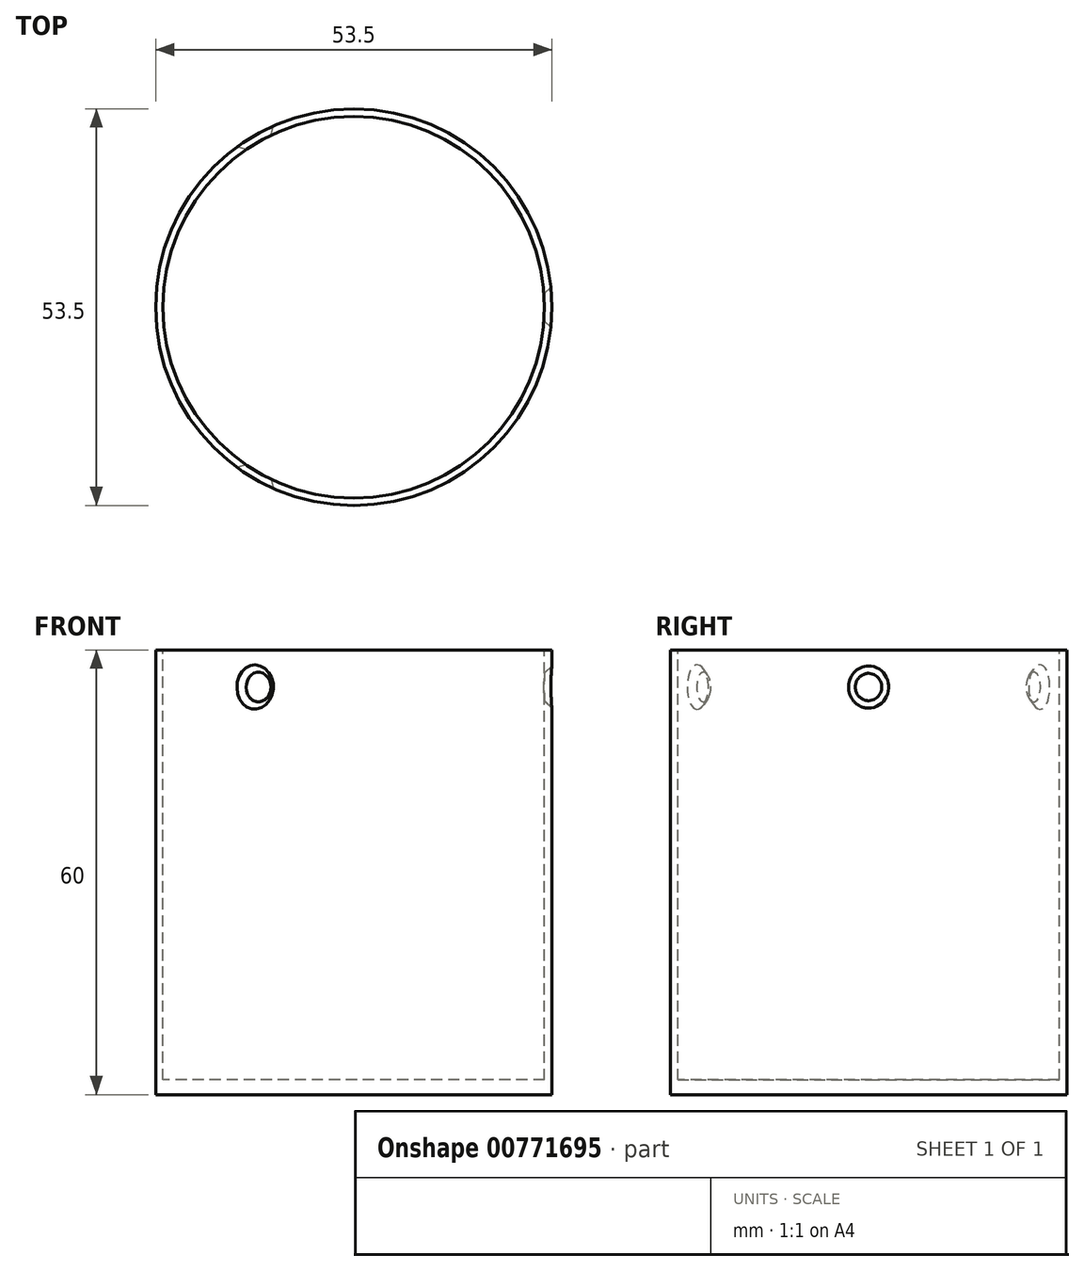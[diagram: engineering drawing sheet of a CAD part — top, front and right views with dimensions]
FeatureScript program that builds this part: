
annotation { "Feature Type Name" : "Feature", "Feature Type Description" : "" }
export const myFeature = defineFeature(function(context is Context, id is Id, definition is map)
    precondition{}
    {
        {
            var Q0;
            Q0=qCreatedBy(makeId("Top.planeOp"),FACE);
            var sketch = newSketch(context, id + "F0", { "sketchPlane" : qUnion([Q0])});
            skCircle(sketch, "E0", {"center": v(0, 0) * mm, "radius": 26.75 * mm});
            skLineSegment(sketch, "E1", {"start": v(0, 0) * mm, "end": v(-13.38, 23.17) * mm});
            skLineSegment(sketch, "E2", {"start": v(0, 0) * mm, "end": v(-13.38, -23.17) * mm});
            skCircle(sketch, "E3", {"center": v(0, 0) * mm, "radius": 25.75 * mm});
            skSolve(sketch);
        }
        {
            var Q0;
            Q0 = qSketchRegion(id + "F0", true);
            var Q1;
            {var subQ0=sQuery(id+"F0.wireOp",EDGE,"E2");var subQ1=sQuery(id+"F0.wireOp",EDGE,"E1");var subQ2=makeQuery(id+"F0.imprint","INTERSECT",VERTEX,{"derivedFrom":[subQ1,subQ0]});Q1=makeQuery(id+"F0.imprint","IMPRINT",FACE,{"disambiguationData":[TD([[makeQuery(id+"F0.imprint","IMPRINT",EDGE,{"disambiguationData":[TD([[subQ2,-1.0]])],"derivedFrom":subQ1}),-1.0]])]});}
            var Q2;
            {var subQ0=sQuery(id+"F0.wireOp",EDGE,"E2");var subQ1=sQuery(id+"F0.wireOp",EDGE,"E1");var subQ2=makeQuery(id+"F0.imprint","INTERSECT",VERTEX,{"derivedFrom":[subQ1,subQ0]});Q2=makeQuery(id+"F0.imprint","IMPRINT",FACE,{"disambiguationData":[TD([[makeQuery(id+"F0.imprint","IMPRINT",EDGE,{"disambiguationData":[TD([[subQ2,-1.0]])],"derivedFrom":subQ1}),1.0]])]});}
            var Q3;
            {var subQ0=sQuery(id+"F0.wireOp",EDGE,"f2nORIOP-7bt3-1o27-wZsQ-XFk8Kn9yNNnm");var subQ1=sQuery(id+"F0.wireOp",EDGE,"E1");var subQ2=makeQuery(id+"F0.imprint","INTERSECT",VERTEX,{"derivedFrom":[subQ1,subQ0]});Q3=makeQuery(id+"F0.imprint","IMPRINT",FACE,{"disambiguationData":[TD([[makeQuery(id+"F0.imprint","IMPRINT",EDGE,{"disambiguationData":[TD([[subQ2,-1.0]])],"derivedFrom":subQ1}),1.0]])]});}
            var Q4;
            {var subQ0=sQuery(id+"F0.wireOp",EDGE,"f2nORIOP-7bt3-1o27-wZsQ-XFk8Kn9yNNnm");var subQ1=sQuery(id+"F0.wireOp",EDGE,"E1");var subQ2=makeQuery(id+"F0.imprint","INTERSECT",VERTEX,{"derivedFrom":[subQ1,subQ0]});Q4=makeQuery(id+"F0.imprint","IMPRINT",FACE,{"disambiguationData":[TD([[makeQuery(id+"F0.imprint","IMPRINT",EDGE,{"disambiguationData":[TD([[subQ2,-1.0]])],"derivedFrom":subQ1}),-1.0]])]});}
            extrude(context, id + "F1", {"entities" : qUnion([Q0, Q1, Q2, Q3, Q4]), "oppositeDirection" : true, "depth" : 60 * mm, "offsetDistance" : 25 * mm});
        }
        {
            var Q0;
            {var subQ0=sQuery(id+"F0.wireOp",EDGE,"E2");var subQ1=sQuery(id+"F0.wireOp",EDGE,"E1");var subQ2=makeQuery(id+"F0.imprint","INTERSECT",VERTEX,{"derivedFrom":[subQ1,subQ0]});Q0=makeQuery(id+"F0.imprint","IMPRINT",FACE,{"disambiguationData":[TD([[makeQuery(id+"F0.imprint","IMPRINT",EDGE,{"disambiguationData":[TD([[subQ2,-1.0]])],"derivedFrom":subQ1}),-1.0]])]});}
            var Q1;
            {var subQ0=sQuery(id+"F0.wireOp",EDGE,"E2");var subQ1=sQuery(id+"F0.wireOp",EDGE,"E1");var subQ2=makeQuery(id+"F0.imprint","INTERSECT",VERTEX,{"derivedFrom":[subQ1,subQ0]});Q1=makeQuery(id+"F0.imprint","IMPRINT",FACE,{"disambiguationData":[TD([[makeQuery(id+"F0.imprint","IMPRINT",EDGE,{"disambiguationData":[TD([[subQ2,-1.0]])],"derivedFrom":subQ1}),1.0]])]});}
            extrude(context, id + "F2", {"entities" : qUnion([Q0, Q1]), "operationType" : NewBodyOperationType.REMOVE, "oppositeDirection" : true, "depth" : 58 * mm, "offsetDistance" : 25 * mm});
        }
        {
            var Q0;
            Q0=qCreatedBy(makeId("Right.planeOp"),FACE);
            cPlane(context, id + "F3", {"entities" : qUnion([Q0]), "cplaneType" : CPlaneType.OFFSET, "offset" : 26.9 * mm, "width" : 150 * mm, "height" : 150 * mm});
        }
        {
            var Q0;
            Q0=sQuery(id+"F0.wireOp",VERTEX,"E1.end");
            var Q1;
            Q1=sQuery(id+"F0.wireOp",EDGE,"E1");
            cPlane(context, id + "F4", {"entities" : qUnion([Q0, Q1]), "cplaneType" : CPlaneType.LINE_POINT, "offset" : 25 * mm, "width" : 150 * mm, "height" : 150 * mm});
        }
        {
            var Q0;
            Q0=sQuery(id+"F0.wireOp",EDGE,"E2");
            var Q1;
            Q1=sQuery(id+"F0.wireOp",VERTEX,"E2.end");
            var Q2;
            Q2 = qBodyType(qCreatedBy(id + "F6" ,EDGE), BodyType.WIRE);
            cPlane(context, id + "F5", {"entities" : qUnion([Q0, Q1, Q2]), "cplaneType" : CPlaneType.LINE_POINT, "offset" : 25 * mm, "width" : 150 * mm, "height" : 150 * mm});
        }
        {
            var Q0;
            Q0=qCreatedBy(id+"F3.planeOp",FACE);
            var sketch = newSketch(context, id + "F6", { "sketchPlane" : qUnion([Q0])});
            skPoint(sketch, "E4", {"position": v(0, -5) * mm});
            skSolve(sketch);
        }
        {
            var Q0;
            Q0=qCreatedBy(id+"F4.planeOp",FACE);
            var sketch = newSketch(context, id + "F7", { "sketchPlane" : qUnion([Q0])});
            skPoint(sketch, "E5", {"position": v(0, -5) * mm});
            skSolve(sketch);
        }
        {
            var Q0;
            Q0=qCreatedBy(id+"F5.planeOp",FACE);
            var sketch = newSketch(context, id + "F8", { "sketchPlane" : qUnion([Q0])});
            skPoint(sketch, "E6", {"position": v(0, -5) * mm});
            skSolve(sketch);
        }
        {
            var Q0;
            Q0=sQuery(id+"F7.wireOp",VERTEX,"E5");
            var Q1;
            Q1=sQuery(id+"F6.wireOp",VERTEX,"E4");
            var Q2;
            Q2=sQuery(id+"F8.wireOp",VERTEX,"E6");
            var Q3;
            Q3=makeQuery(id+"F1.opExtrude","SWEPT_BODY",BODY,{"disambiguationData":[OSD([sQuery(id+"F0.wireOp",EDGE,"E0")])]});
            hole(context, id + "F9", {"style" : HoleStyle.C_SINK, "endStyle" : HoleEndStyle.BLIND, "holeDiameter" : 3.2 * mm, "cSinkDiameter" : 6 * mm, "cSinkAngle" : 90 * degree, "majorDiameter" : 3 * mm, "holeDepth" : 4 * mm, "isTappedThrough" : true, "tappedDepth" : 2.5 * mm, "tapClearance" : 3, "startFromSketch" : true, "locations" : qUnion([Q0, Q1, Q2]), "scope" : qUnion([Q3])});
        }
    });
